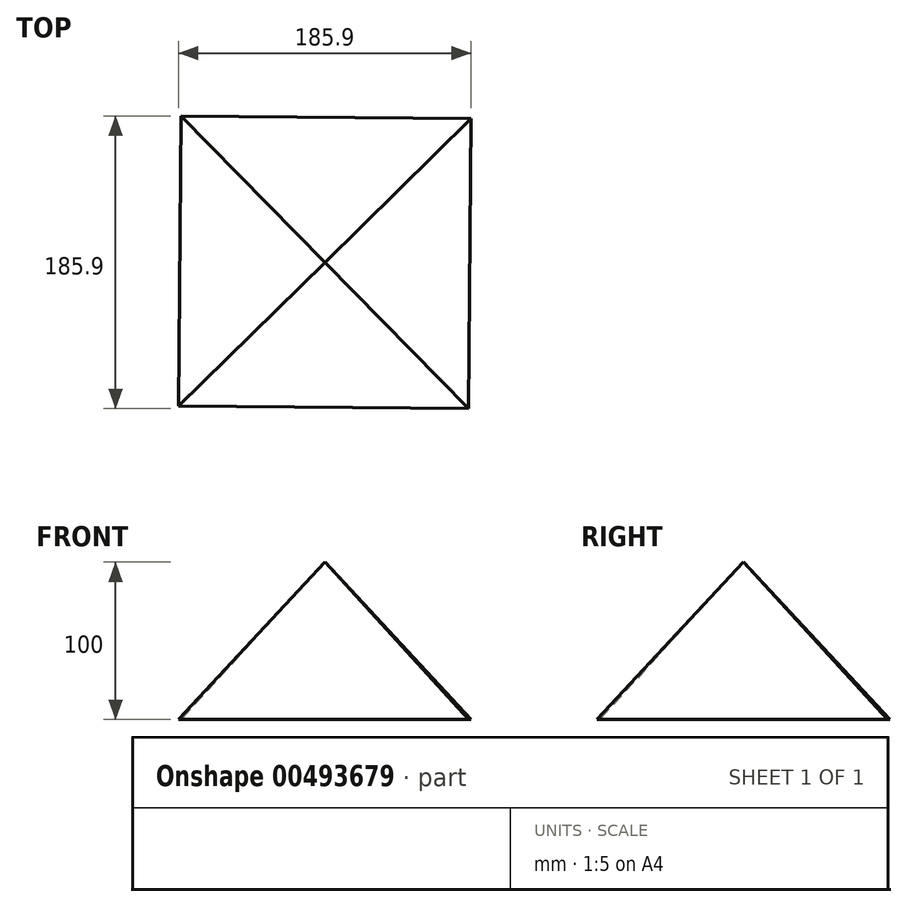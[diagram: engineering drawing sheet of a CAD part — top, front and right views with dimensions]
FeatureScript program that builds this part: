
annotation { "Feature Type Name" : "Feature", "Feature Type Description" : "" }
export const myFeature = defineFeature(function(context is Context, id is Id, definition is map)
    precondition{}
    {
        {
            var Q0;
            Q0=qCreatedBy(makeId("Top.planeOp"),FACE);
            var sketch = newSketch(context, id + "F0", { "sketchPlane" : qUnion([Q0])});
            skCircle(sketch, "E0.cCircle", {"center": v(0, 0) * mm, "radius": 130.34 * mm, "construction": true});
            skLineSegment(sketch, "E0.0", {"start": v(-92.95, -91.37) * mm, "end": v(-91.37, 92.95) * mm});
            skLineSegment(sketch, "E0.1", {"start": v(-91.37, 92.95) * mm, "end": v(92.95, 91.37) * mm});
            skLineSegment(sketch, "E0.2", {"start": v(92.95, 91.37) * mm, "end": v(91.37, -92.95) * mm});
            skLineSegment(sketch, "E0.3", {"start": v(91.37, -92.95) * mm, "end": v(-92.95, -91.37) * mm});
            skSolve(sketch);
        }
        {
            var Q0;
            Q0=qCreatedBy(makeId("Top.planeOp"),FACE);
            cPlane(context, id + "F1", {"entities" : qUnion([Q0]), "cplaneType" : CPlaneType.OFFSET, "offset" : 100 * mm, "width" : 150 * mm, "height" : 150 * mm});
        }
        {
            var Q0;
            Q0=qCreatedBy(id+"F1.planeOp",FACE);
            var sketch = newSketch(context, id + "F2", { "sketchPlane" : qUnion([Q0])});
            skPoint(sketch, "E1", {"position": v(0, 0) * mm});
            skSolve(sketch);
        }
        {
            var Q0;
            Q0=sQuery(id+"F2.wireOp",VERTEX,"E1");
            var Q1;
            Q1=makeQuery(id+"F0.imprint","IMPRINT",FACE,{"disambiguationData":[TD([[makeQuery(id+"F0.imprint","IMPRINT",EDGE,{"derivedFrom":sQuery(id+"F0.wireOp",EDGE,"E0.0")}),-1.0]])]});
            loft(context, id + "F3", {"sheetProfilesArray" : [{ "sheetProfileEntities" : qUnion([Q0]) }, { "sheetProfileEntities" : qUnion([Q1]) }]});
        }
    });
